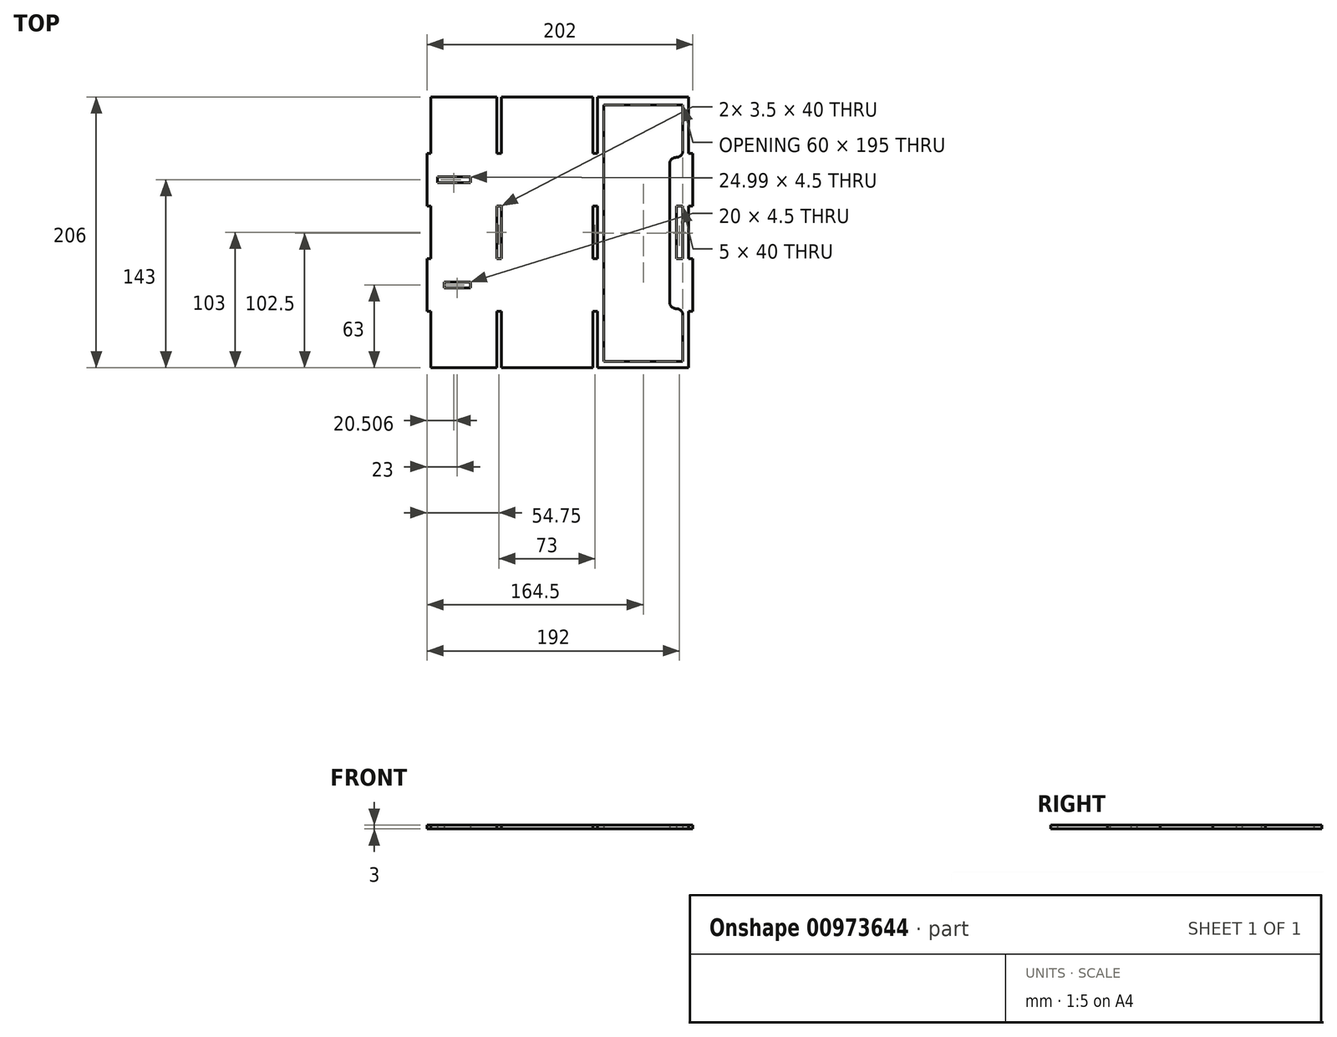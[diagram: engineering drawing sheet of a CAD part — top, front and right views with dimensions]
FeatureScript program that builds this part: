
annotation { "Feature Type Name" : "Feature", "Feature Type Description" : "" }
export const myFeature = defineFeature(function(context is Context, id is Id, definition is map)
    precondition{}
    {
        {
            var Q0;
            Q0=qCreatedBy(makeId("Top.planeOp"),FACE);
            var sketch = newSketch(context, id + "F0", { "sketchPlane" : qUnion([Q0])});
            skLineSegment(sketch, "E0", {"start": v(202, -200) * mm, "end": v(0, -200) * mm});
            skLineSegment(sketch, "E1", {"start": v(0, -200) * mm, "end": v(0, 6) * mm});
            skLineSegment(sketch, "E2", {"start": v(0, 6) * mm, "end": v(202, 6) * mm});
            skLineSegment(sketch, "E3", {"start": v(202, -200) * mm, "end": v(202, 6) * mm});
            skLineSegment(sketch, "E4", {"start": v(0, -200) * mm, "end": v(3, -200) * mm});
            skLineSegment(sketch, "E5", {"start": v(3, -200) * mm, "end": v(3, -157) * mm});
            skLineSegment(sketch, "E6", {"start": v(3, -157) * mm, "end": v(0, -157) * mm});
            skLineSegment(sketch, "E7", {"start": v(0, -157) * mm, "end": v(0, -117) * mm});
            skLineSegment(sketch, "E8", {"start": v(0, -117) * mm, "end": v(3, -117) * mm});
            skLineSegment(sketch, "E9", {"start": v(3, -117) * mm, "end": v(3, -77) * mm});
            skLineSegment(sketch, "E10", {"start": v(3, -77) * mm, "end": v(0, -77) * mm});
            skLineSegment(sketch, "E11", {"start": v(0, -77) * mm, "end": v(0, -37) * mm});
            skLineSegment(sketch, "E12", {"start": v(0, -37) * mm, "end": v(3, -37) * mm});
            skLineSegment(sketch, "E13", {"start": v(3, -37) * mm, "end": v(3, 6) * mm});
            skLineSegment(sketch, "E14", {"start": v(3, -200) * mm, "end": v(53, -200) * mm});
            skLineSegment(sketch, "E15", {"start": v(53, -200) * mm, "end": v(56, -200) * mm});
            skLineSegment(sketch, "E16", {"start": v(53, -157) * mm, "end": v(53, -200) * mm});
            skLineSegment(sketch, "E17", {"start": v(53, -117) * mm, "end": v(53, -77) * mm});
            skLineSegment(sketch, "E18", {"start": v(53, 6) * mm, "end": v(53, -37) * mm});
            skLineSegment(sketch, "E19", {"start": v(56, -200) * mm, "end": v(126, -200) * mm});
            skLineSegment(sketch, "E20", {"start": v(126, -200) * mm, "end": v(126, -157) * mm});
            skLineSegment(sketch, "E21", {"start": v(126, -117) * mm, "end": v(126, -77) * mm});
            skLineSegment(sketch, "E22", {"start": v(126, -37) * mm, "end": v(126, 6) * mm});
            skLineSegment(sketch, "E23", {"start": v(202, -200) * mm, "end": v(199, -200) * mm});
            skLineSegment(sketch, "E24", {"start": v(199, -200) * mm, "end": v(199, -157) * mm});
            skLineSegment(sketch, "E25", {"start": v(199, -157) * mm, "end": v(202, -157) * mm});
            skLineSegment(sketch, "E26", {"start": v(199, -117) * mm, "end": v(199, -77) * mm});
            skLineSegment(sketch, "E27", {"start": v(199, -77) * mm, "end": v(202, -77) * mm});
            skLineSegment(sketch, "E28", {"start": v(199, -117) * mm, "end": v(202, -117) * mm});
            skLineSegment(sketch, "E29", {"start": v(199, -37) * mm, "end": v(199, 6) * mm});
            skLineSegment(sketch, "E30", {"start": v(199, -37) * mm, "end": v(202, -37) * mm});
            skLineSegment(sketch, "E31", {"start": v(53, -157) * mm, "end": v(56.5, -157) * mm});
            skLineSegment(sketch, "E32", {"start": v(56.5, -157) * mm, "end": v(56.5, -200) * mm});
            skLineSegment(sketch, "E33", {"start": v(53, -117) * mm, "end": v(56.5, -117) * mm});
            skLineSegment(sketch, "E34", {"start": v(56.5, -117) * mm, "end": v(56.5, -77) * mm});
            skLineSegment(sketch, "E35", {"start": v(56.5, -77) * mm, "end": v(53, -77) * mm});
            skLineSegment(sketch, "E36", {"start": v(56.5, -37) * mm, "end": v(56.5, 6) * mm});
            skLineSegment(sketch, "E37", {"start": v(53, -37) * mm, "end": v(56.5, -37) * mm});
            skLineSegment(sketch, "E38", {"start": v(126, -157) * mm, "end": v(129.5, -157) * mm});
            skLineSegment(sketch, "E39", {"start": v(129.5, -157) * mm, "end": v(129.5, -200) * mm});
            skLineSegment(sketch, "E40", {"start": v(126, -117) * mm, "end": v(129.5, -117) * mm});
            skLineSegment(sketch, "E41", {"start": v(129.5, -117) * mm, "end": v(129.5, -77) * mm});
            skLineSegment(sketch, "E42", {"start": v(129.5, -77) * mm, "end": v(126, -77) * mm});
            skLineSegment(sketch, "E43", {"start": v(129.5, -37) * mm, "end": v(129.5, 6) * mm});
            skLineSegment(sketch, "E44", {"start": v(126, -37) * mm, "end": v(129.5, -37) * mm});
            skLineSegment(sketch, "E45", {"start": v(134.5, -97) * mm, "end": v(134.5, 0) * mm});
            skLineSegment(sketch, "E46", {"start": v(134.5, 0) * mm, "end": v(194.5, 0) * mm});
            skLineSegment(sketch, "E47", {"start": v(194.5, -195) * mm, "end": v(134.5, -195) * mm});
            skLineSegment(sketch, "E48", {"start": v(134.5, -195) * mm, "end": v(134.5, -97) * mm});
            skLineSegment(sketch, "E49", {"start": v(194.5, -195) * mm, "end": v(194.5, -155) * mm});
            skLineSegment(sketch, "E50", {"start": v(194.5, 0) * mm, "end": v(194.5, -40) * mm});
            skLineSegment(sketch, "E51", {"start": v(194.5, -40) * mm, "end": v(184.5, -40) * mm});
            skLineSegment(sketch, "E52", {"start": v(184.5, -40) * mm, "end": v(184.5, -155) * mm});
            skLineSegment(sketch, "E53", {"start": v(184.5, -155) * mm, "end": v(194.5, -155) * mm});
            skLineSegment(sketch, "E54", {"start": v(194.5, -117) * mm, "end": v(194.5, -77) * mm});
            skLineSegment(sketch, "E55", {"start": v(194.5, -77) * mm, "end": v(189.5, -77) * mm});
            skLineSegment(sketch, "E56", {"start": v(189.5, -77) * mm, "end": v(189.5, -117) * mm});
            skLineSegment(sketch, "E57", {"start": v(189.5, -117) * mm, "end": v(194.5, -117) * mm});
            skPoint(sketch, "E58.startSnap0", {"position": v(0, -137) * mm});
            skLineSegment(sketch, "E59", {"start": v(33, -137) * mm, "end": v(33, -134.75) * mm});
            skLineSegment(sketch, "E60", {"start": v(33, -134.75) * mm, "end": v(13, -134.75) * mm});
            skLineSegment(sketch, "E61", {"start": v(13, -134.75) * mm, "end": v(13, -139.25) * mm});
            skLineSegment(sketch, "E62", {"start": v(13, -139.25) * mm, "end": v(33, -139.25) * mm});
            skLineSegment(sketch, "E63", {"start": v(33, -139.25) * mm, "end": v(33, -137) * mm});
            skLineSegment(sketch, "E64", {"start": v(33, -57) * mm, "end": v(33, -54.75) * mm});
            skPoint(sketch, "E64.startSnap0", {"position": v(0, -57) * mm});
            skLineSegment(sketch, "E65", {"start": v(33, -54.75) * mm, "end": v(8.01, -54.75) * mm});
            skLineSegment(sketch, "E66", {"start": v(33, -57) * mm, "end": v(33, -59.25) * mm});
            skLineSegment(sketch, "E67", {"start": v(33, -59.25) * mm, "end": v(8.01, -59.25) * mm});
            skLineSegment(sketch, "E68", {"start": v(8.01, -59.25) * mm, "end": v(8.01, -54.75) * mm});
            skSolve(sketch);
        }
        {
            var Q0;
            {var subQ22=sQuery(id+"F0.wireOp",EDGE,"E5");Q0=makeQuery(id+"F0.imprint","IMPRINT",FACE,{"disambiguationData":[TD([[makeQuery(id+"F0.imprint","IMPRINT",EDGE,{"derivedFrom":subQ22}),-1.0]])]});}
            extrude(context, id + "F1", {"entities" : qUnion([Q0]), "depth" : 3 * mm, "offsetDistance" : 25 * mm});
        }
        {
            var Q0;
            Q0=makeQuery(id+"F1.opExtrude","SWEPT_EDGE",EDGE,{"disambiguationData":[OSD([sQuery(id+"F0.wireOp",EDGE,"E50"),sQuery(id+"F0.wireOp",EDGE,"E51")])]});
            var Q1;
            Q1=makeQuery(id+"F1.opExtrude","SWEPT_EDGE",EDGE,{"disambiguationData":[OSD([sQuery(id+"F0.wireOp",EDGE,"E51"),sQuery(id+"F0.wireOp",EDGE,"E52")])]});
            fillet(context, id + "F2", {"entities" : qUnion([Q0, Q1]), "radius" : 5 * mm, "tangentPropagation" : true, "allowEdgeOverflow" : false});
        }
        {
            var Q0;
            Q0=makeQuery(id+"F1.opExtrude","SWEPT_EDGE",EDGE,{"disambiguationData":[OSD([sQuery(id+"F0.wireOp",EDGE,"E49"),sQuery(id+"F0.wireOp",EDGE,"E53")])]});
            var Q1;
            Q1=makeQuery(id+"F1.opExtrude","SWEPT_EDGE",EDGE,{"disambiguationData":[OSD([sQuery(id+"F0.wireOp",EDGE,"E52"),sQuery(id+"F0.wireOp",EDGE,"E53")])]});
            fillet(context, id + "F3", {"entities" : qUnion([Q0, Q1]), "radius" : 5 * mm, "tangentPropagation" : true, "allowEdgeOverflow" : false});
        }
    });
